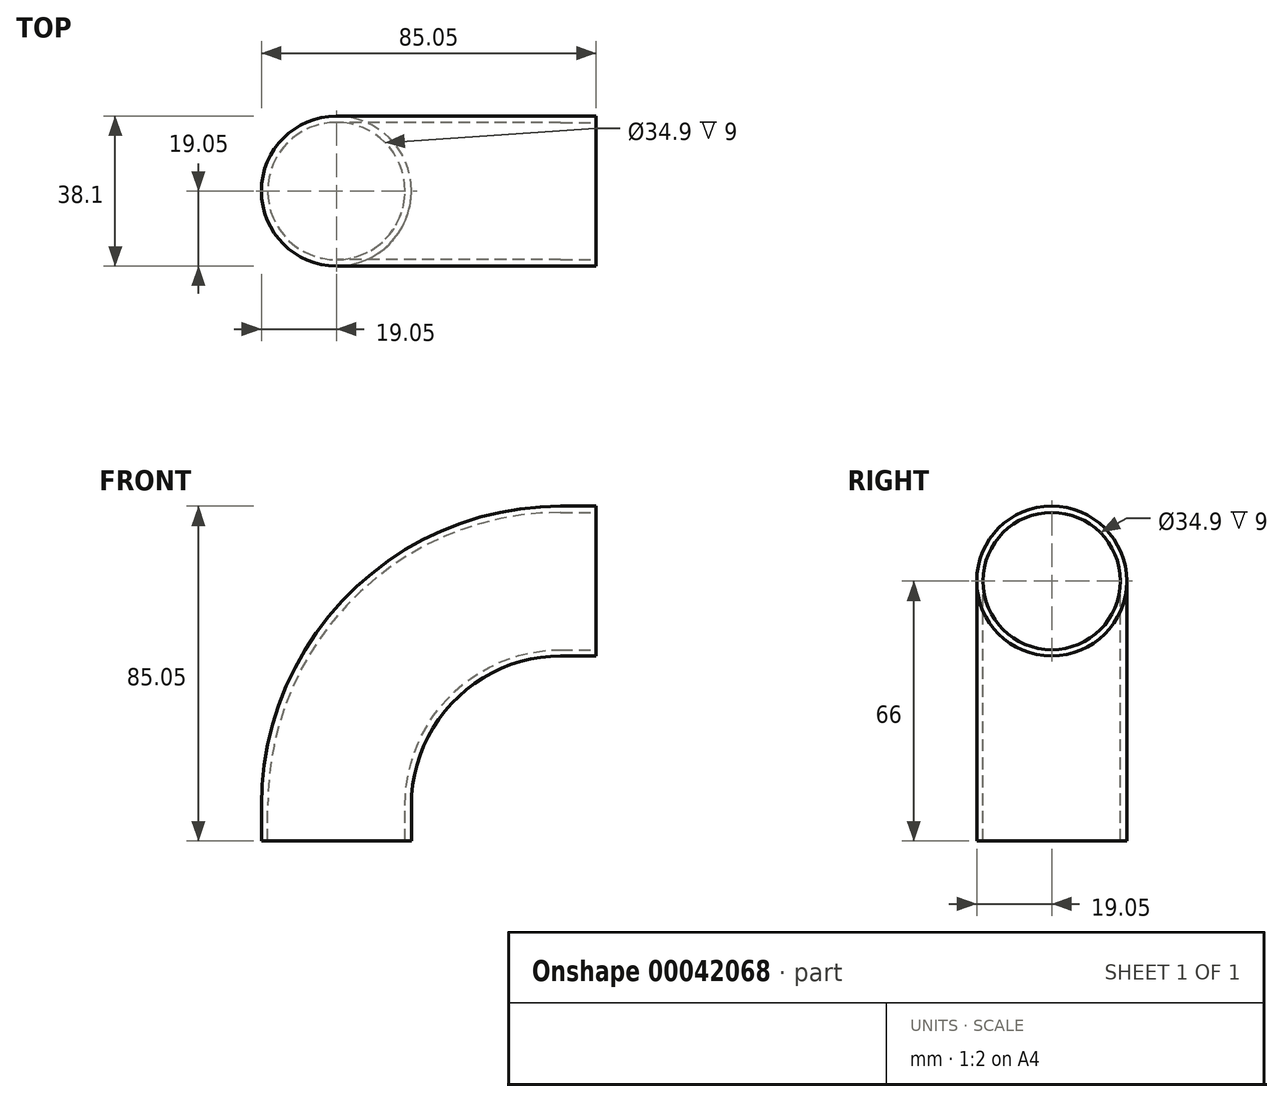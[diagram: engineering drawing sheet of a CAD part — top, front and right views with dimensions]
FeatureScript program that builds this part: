
annotation { "Feature Type Name" : "Feature", "Feature Type Description" : "" }
export const myFeature = defineFeature(function(context is Context, id is Id, definition is map)
    precondition{}
    {
        {
            var Q0;
            Q0=qCreatedBy(makeId("Front.planeOp"),FACE);
            var sketch = newSketch(context, id + "F0", { "sketchPlane" : qUnion([Q0])});
            skLineSegment(sketch, "E0", {"start": v(0, 0) * mm, "end": v(0, 9) * mm});
            skArc(sketch, "E1", {"start": v(57, 66) * mm, "mid": v(16.7, 49.3) * mm, "end": v(0, 9) * mm});
            skLineSegment(sketch, "E2", {"start": v(57, 66) * mm, "end": v(66, 66) * mm});
            skSolve(sketch);
        }
        {
            var Q0;
            Q0=qCreatedBy(makeId("Top.planeOp"),FACE);
            var sketch = newSketch(context, id + "F1", { "sketchPlane" : qUnion([Q0])});
            skCircle(sketch, "E3", {"center": v(0, 0) * mm, "radius": 19.05 * mm});
            skCircle(sketch, "E4.0", {"center": v(0, 0) * mm, "radius": 17.45 * mm});
            skSolve(sketch);
        }
        {
            var Q0;
            Q0=makeQuery(id+"F1.imprint","IMPRINT",FACE,{"disambiguationData":[TD([[makeQuery(id+"F1.imprint","IMPRINT",EDGE,{"derivedFrom":sQuery(id+"F1.wireOp",EDGE,"E3")}),1.0]])]});
            var Q1;
            Q1=sQuery(id+"F0.wireOp",EDGE,"E1");
            var Q2;
            Q2=sQuery(id+"F0.wireOp",EDGE,"E0");
            var Q3;
            Q3=sQuery(id+"F0.wireOp",EDGE,"E2");
            sweep(context, id + "F2", {"profiles" : qUnion([Q0]), "path" : qUnion([Q1, Q2, Q3])});
        }
    });
